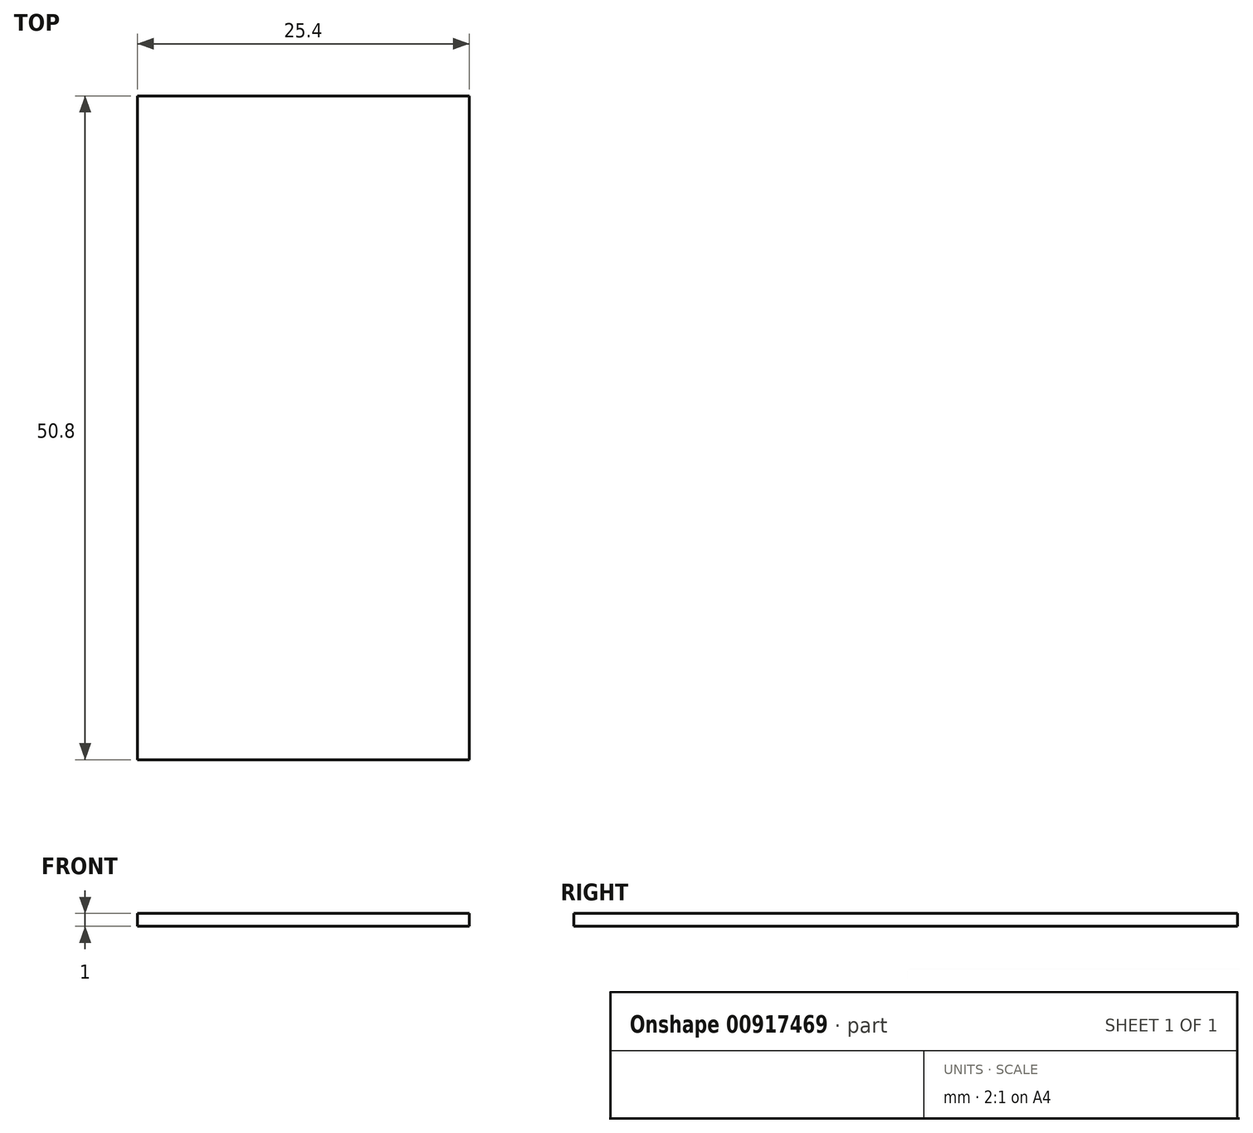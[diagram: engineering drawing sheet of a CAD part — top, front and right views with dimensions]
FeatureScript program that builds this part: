
annotation { "Feature Type Name" : "Feature", "Feature Type Description" : "" }
export const myFeature = defineFeature(function(context is Context, id is Id, definition is map)
    precondition{}
    {
        {
            var Q0;
            Q0=qCreatedBy(makeId("Top.planeOp"),FACE);
            var sketch = newSketch(context, id + "F0", { "sketchPlane" : qUnion([Q0])});
            skLineSegment(sketch, "E0.bottom", {"start": v(-50.04, -26.05) * mm, "end": v(-24.64, -26.05) * mm});
            skLineSegment(sketch, "E0.top", {"start": v(-50.04, 24.75) * mm, "end": v(-24.64, 24.75) * mm});
            skLineSegment(sketch, "E0.left", {"start": v(-50.04, -26.05) * mm, "end": v(-50.04, 24.75) * mm});
            skLineSegment(sketch, "E0.right", {"start": v(-24.64, -26.05) * mm, "end": v(-24.64, 24.75) * mm});
            skSolve(sketch);
        }
        {
            var Q0;
            Q0=makeQuery(id+"F0.imprint","IMPRINT",FACE,{"disambiguationData":[TD([[makeQuery(id+"F0.imprint","IMPRINT",EDGE,{"derivedFrom":sQuery(id+"F0.wireOp",EDGE,"E0.bottom")}),1.0]])]});
            extrude(context, id + "F1", {"entities" : qUnion([Q0]), "depth" : 1 * mm, "offsetDistance" : 25.4 * mm});
        }
    });
